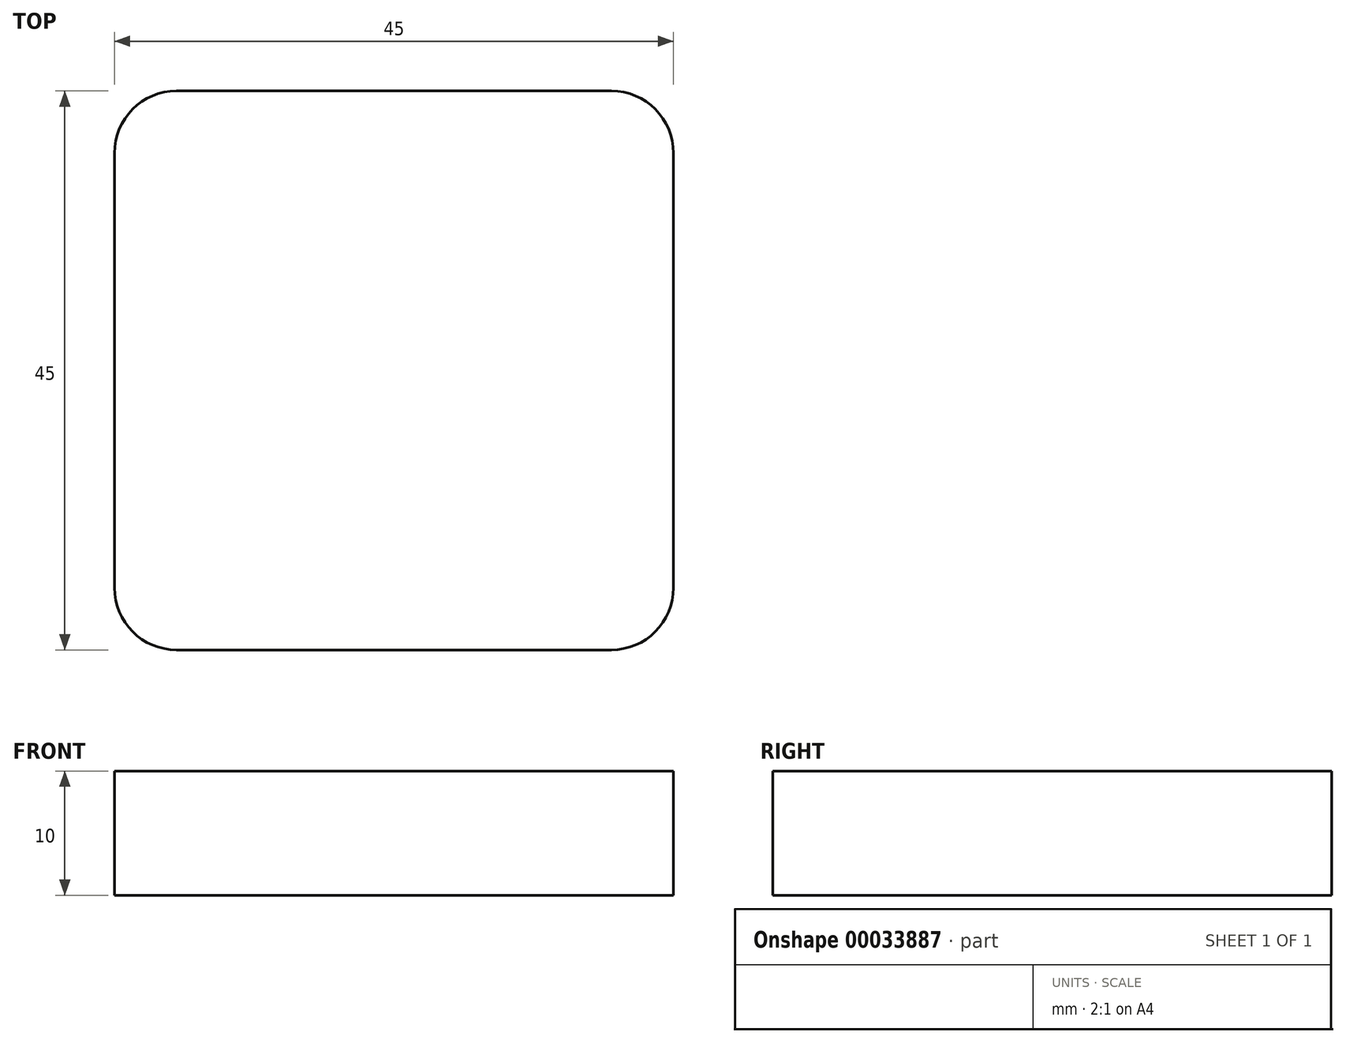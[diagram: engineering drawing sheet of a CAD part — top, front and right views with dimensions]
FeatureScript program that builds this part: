
annotation { "Feature Type Name" : "Feature", "Feature Type Description" : "" }
export const myFeature = defineFeature(function(context is Context, id is Id, definition is map)
    precondition{}
    {
        {
            var Q0;
            Q0=qCreatedBy(makeId("Top.planeOp"),FACE);
            var sketch = newSketch(context, id + "F0", { "sketchPlane" : qUnion([Q0])});
            skLineSegment(sketch, "E0.rect.bottom", {"start": v(-22.5, 22.5) * mm, "end": v(22.5, 22.5) * mm});
            skLineSegment(sketch, "E0.rect.top", {"start": v(-22.5, -22.5) * mm, "end": v(22.5, -22.5) * mm});
            skLineSegment(sketch, "E0.rect.left", {"start": v(-22.5, 22.5) * mm, "end": v(-22.5, -22.5) * mm});
            skLineSegment(sketch, "E0.rect.right", {"start": v(22.5, 22.5) * mm, "end": v(22.5, -22.5) * mm});
            skPoint(sketch, "E0.rect.middle", {"position": v(0, 0) * mm});
            skSolve(sketch);
        }
        {
            var Q0;
            Q0 = qSketchRegion(id + "F0", true);
            extrude(context, id + "F1", {"entities" : qUnion([Q0]), "depth" : 10 * mm});
        }
        {
            var Q0;
            Q0=makeQuery(id+"F1.opExtrude","SWEPT_EDGE",EDGE,{"disambiguationData":[OSD([sQuery(id+"F0.wireOp",EDGE,"E0.rect.top"),sQuery(id+"F0.wireOp",EDGE,"E0.rect.right")])]});
            fillet(context, id + "F2", {"entities" : qUnion([Q0]), "radius" : 5 * mm, "tangentPropagation" : true, "allowEdgeOverflow" : false});
        }
        {
            var Q0;
            Q0=makeQuery(id+"F1.opExtrude","SWEPT_EDGE",EDGE,{"disambiguationData":[OSD([sQuery(id+"F0.wireOp",EDGE,"E0.rect.bottom"),sQuery(id+"F0.wireOp",EDGE,"E0.rect.right")])]});
            fillet(context, id + "F3", {"entities" : qUnion([Q0]), "radius" : 5 * mm, "tangentPropagation" : true, "allowEdgeOverflow" : false});
        }
        {
            var Q0;
            Q0=makeQuery(id+"F1.opExtrude","SWEPT_EDGE",EDGE,{"disambiguationData":[OSD([sQuery(id+"F0.wireOp",EDGE,"E0.rect.top"),sQuery(id+"F0.wireOp",EDGE,"E0.rect.left")])]});
            fillet(context, id + "F4", {"entities" : qUnion([Q0]), "radius" : 5 * mm, "tangentPropagation" : true, "allowEdgeOverflow" : false});
        }
        {
            var Q0;
            Q0=makeQuery(id+"F1.opExtrude","SWEPT_EDGE",EDGE,{"disambiguationData":[OSD([sQuery(id+"F0.wireOp",EDGE,"E0.rect.bottom"),sQuery(id+"F0.wireOp",EDGE,"E0.rect.left")])]});
            fillet(context, id + "F5", {"entities" : qUnion([Q0]), "radius" : 5 * mm, "tangentPropagation" : true, "allowEdgeOverflow" : false});
        }
    });
